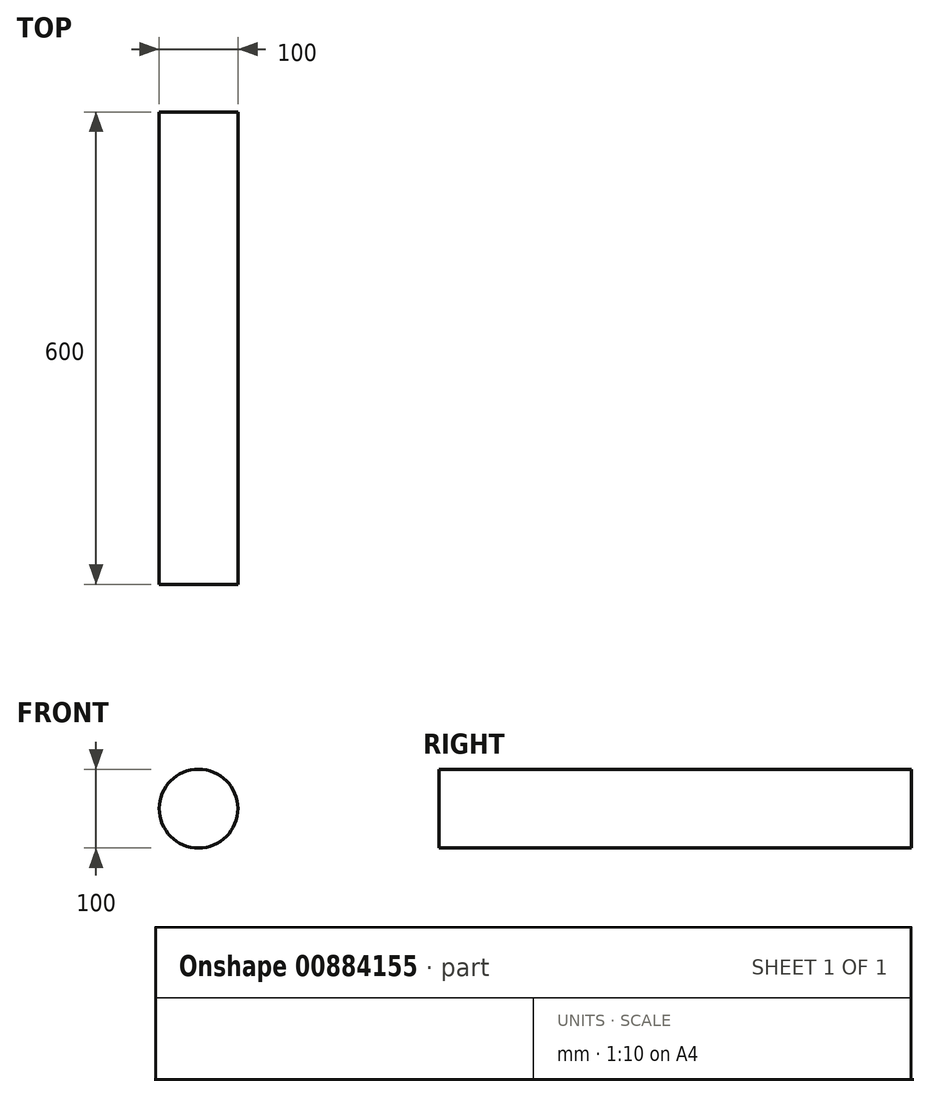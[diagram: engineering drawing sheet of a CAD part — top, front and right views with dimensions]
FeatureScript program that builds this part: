
annotation { "Feature Type Name" : "Feature", "Feature Type Description" : "" }
export const myFeature = defineFeature(function(context is Context, id is Id, definition is map)
    precondition{}
    {
        {
            var Q0;
            Q0=qCreatedBy(makeId("Front.planeOp"),FACE);
            var sketch = newSketch(context, id + "F0", { "sketchPlane" : qUnion([Q0])});
            skCircle(sketch, "E0", {"center": v(0, 0) * mm, "radius": 50 * mm});
            skSolve(sketch);
        }
        {
            var Q0;
            Q0=makeQuery(id+"F0.imprint","IMPRINT",FACE,{"disambiguationData":[TD([[makeQuery(id+"F0.imprint","IMPRINT",EDGE,{"derivedFrom":sQuery(id+"F0.wireOp",EDGE,"E0")}),1.0]])]});
            extrude(context, id + "F1", {"entities" : qUnion([Q0]), "depth" : 600 * mm, "offsetDistance" : 25 * mm});
        }
    });
